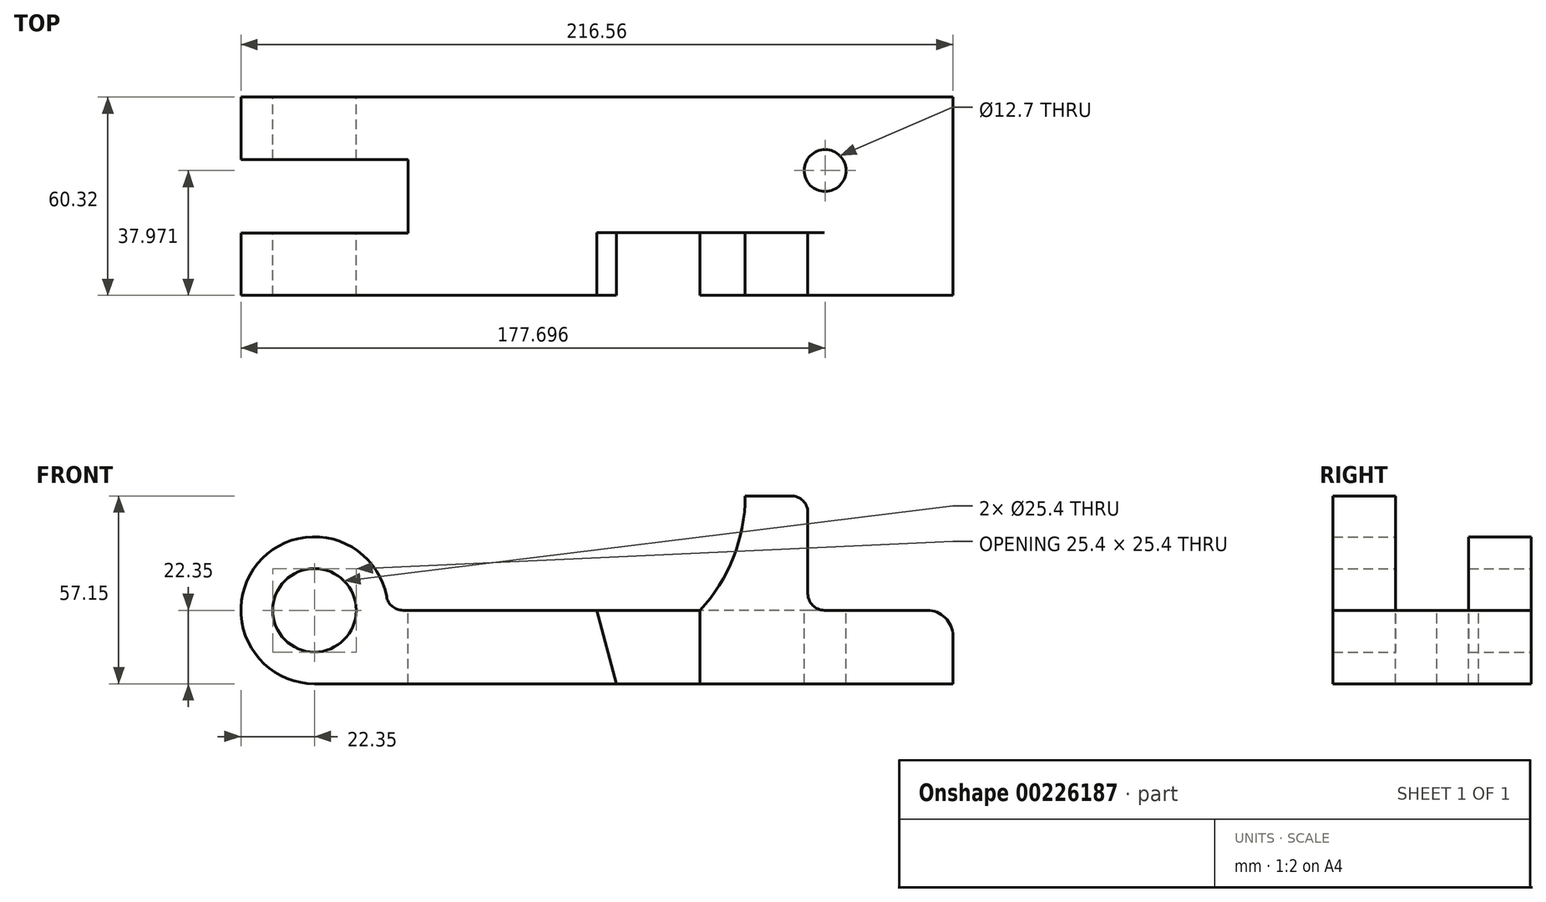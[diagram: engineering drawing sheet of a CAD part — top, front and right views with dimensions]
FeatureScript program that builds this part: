
annotation { "Feature Type Name" : "Feature", "Feature Type Description" : "" }
export const myFeature = defineFeature(function(context is Context, id is Id, definition is map)
    precondition{}
    {
        {
            var Q0;
            Q0=qCreatedBy(makeId("Front.planeOp"),FACE);
            var sketch = newSketch(context, id + "F0", { "sketchPlane" : qUnion([Q0])});
            skCircle(sketch, "E0", {"center": v(0, 0) * mm, "radius": 12.7 * mm});
            skArc(sketch, "E1", {"start": v(22.35, 0) * mm, "mid": v(-15.8, 15.8) * mm, "end": v(0, -22.35) * mm});
            skLineSegment(sketch, "E2", {"start": v(0, -22.35) * mm, "end": v(91.85, -22.35) * mm});
            skLineSegment(sketch, "E3", {"start": v(91.85, -22.35) * mm, "end": v(117.25, -22.35) * mm});
            skLineSegment(sketch, "E4", {"start": v(117.25, -22.35) * mm, "end": v(194.2, -22.35) * mm});
            skLineSegment(sketch, "E5", {"start": v(194.2, -22.35) * mm, "end": v(194.2, 0) * mm});
            skLineSegment(sketch, "E6", {"start": v(22.35, 0) * mm, "end": v(85.85, 0) * mm});
            skLineSegment(sketch, "E7", {"start": v(194.2, 0) * mm, "end": v(150.09, 0) * mm});
            skLineSegment(sketch, "E8", {"start": v(150.09, 0) * mm, "end": v(150.09, 34.8) * mm});
            skLineSegment(sketch, "E9", {"start": v(150.09, 34.8) * mm, "end": v(131.04, 34.8) * mm});
            skLineSegment(sketch, "E10", {"start": v(117.25, -22.35) * mm, "end": v(117.25, 0) * mm});
            skLineSegment(sketch, "E11", {"start": v(85.85, 0) * mm, "end": v(117.25, 0) * mm});
            skLineSegment(sketch, "E12", {"start": v(91.85, -22.35) * mm, "end": v(85.85, 0) * mm});
            skArc(sketch, "E13", {"start": v(117.25, 0) * mm, "mid": v(127.46, 16.08) * mm, "end": v(131.04, 34.8) * mm});
            skSolve(sketch);
        }
        {
            var Q0;
            Q0=makeQuery(id+"F0.imprint","IMPRINT",FACE,{"disambiguationData":[TD([[makeQuery(id+"F0.imprint","IMPRINT",EDGE,{"derivedFrom":sQuery(id+"F0.wireOp",EDGE,"E0")}),-1.0]])]});
            var Q1;
            Q1=makeQuery(id+"F0.imprint","IMPRINT",FACE,{"disambiguationData":[TD([[makeQuery(id+"F0.imprint","IMPRINT",EDGE,{"derivedFrom":sQuery(id+"F0.wireOp",EDGE,"E4")}),1.0]])]});
            var Q2;
            Q2=makeQuery(id+"F0.imprint","IMPRINT",FACE,{"disambiguationData":[TD([[makeQuery(id+"F0.imprint","IMPRINT",EDGE,{"derivedFrom":sQuery(id+"F0.wireOp",EDGE,"E3")}),1.0]])]});
            extrude(context, id + "F11", {"entities" : qUnion([Q0, Q1, Q2]), "endBound" : BoundingType.SYMMETRIC, "depth" : 60.32 * mm});
        }
        {
            var Q0;
            Q0=makeQuery(id+"F11.opExtrude","CAP_FACE",FACE,{"disambiguationData":[OSD([sQuery(id+"F0.wireOp",EDGE,"E0"),sQuery(id+"F0.wireOp",EDGE,"E1"),sQuery(id+"F0.wireOp",EDGE,"E2"),sQuery(id+"F0.wireOp",EDGE,"E3"),sQuery(id+"F0.wireOp",EDGE,"E4"),sQuery(id+"F0.wireOp",EDGE,"E5"),sQuery(id+"F0.wireOp",EDGE,"E6"),sQuery(id+"F0.wireOp",EDGE,"E7"),sQuery(id+"F0.wireOp",EDGE,"E8"),sQuery(id+"F0.wireOp",EDGE,"E9"),sQuery(id+"F0.wireOp",EDGE,"E11"),sQuery(id+"F0.wireOp",EDGE,"E13")])],"isStart":false});
            var sketch = newSketch(context, id + "F1", { "sketchPlane" : qUnion([Q0])});
            skPoint(sketch, "E14.0", {"position": v(91.85, -22.35) * mm});
            skPoint(sketch, "E15.0", {"position": v(85.85, 0) * mm});
            skPoint(sketch, "E16.0", {"position": v(117.25, -22.35) * mm});
            skPoint(sketch, "E17.0", {"position": v(117.25, 0) * mm});
            skLineSegment(sketch, "E18.0", {"start": v(85.85, 0) * mm, "end": v(117.25, 0) * mm});
            skLineSegment(sketch, "E19.0", {"start": v(91.85, -22.35) * mm, "end": v(117.25, -22.35) * mm});
            skLineSegment(sketch, "E20", {"start": v(91.85, -22.35) * mm, "end": v(85.85, 0) * mm});
            skLineSegment(sketch, "E21", {"start": v(117.25, -22.35) * mm, "end": v(117.25, 0) * mm});
            skSolve(sketch);
        }
        {
            var Q0;
            Q0 = qSketchRegion(id + "F1", true);
            extrude(context, id + "F2", {"entities" : qUnion([Q0]), "operationType" : NewBodyOperationType.REMOVE, "oppositeDirection" : true, "depth" : 19.05 * mm});
        }
        {
            var Q0;
            Q0=makeQuery(id+"F11.opExtrude","CAP_FACE",FACE,{"disambiguationData":[OSD([sQuery(id+"F0.wireOp",EDGE,"E0"),sQuery(id+"F0.wireOp",EDGE,"E1"),sQuery(id+"F0.wireOp",EDGE,"E2"),sQuery(id+"F0.wireOp",EDGE,"E3"),sQuery(id+"F0.wireOp",EDGE,"E4"),sQuery(id+"F0.wireOp",EDGE,"E5"),sQuery(id+"F0.wireOp",EDGE,"E6"),sQuery(id+"F0.wireOp",EDGE,"E7"),sQuery(id+"F0.wireOp",EDGE,"E8"),sQuery(id+"F0.wireOp",EDGE,"E9"),sQuery(id+"F0.wireOp",EDGE,"E11"),sQuery(id+"F0.wireOp",EDGE,"E13")])],"isStart":true});
            var sketch = newSketch(context, id + "F3", { "sketchPlane" : qUnion([Q0])});
            skPoint(sketch, "E22.0", {"position": v(-150.09, 0) * mm});
            skPoint(sketch, "E23.0", {"position": v(-117.25, 0) * mm});
            skLineSegment(sketch, "E24", {"start": v(-150.09, 0) * mm, "end": v(-117.25, 0) * mm});
            skSolve(sketch);
        }
        {
            var Q0;
            Q0 = qSketchRegion(id + "F3", true);
            var Q1;
            Q1=makeQuery(id+"F3.imprint","IMPRINT",FACE,{"disambiguationData":[TD([[makeQuery(id+"F3.imprint","IMPRINT",EDGE,{"derivedFrom":sQuery(id+"F3.wireOp",EDGE,"E24")}),1.0]])]});
            extrude(context, id + "F4", {"entities" : qUnion([Q0, Q1]), "operationType" : NewBodyOperationType.REMOVE, "oppositeDirection" : true, "depth" : 41.27 * mm});
        }
        {
            var Q0;
            Q0=makeQuery(id+"F11.opExtrude","SWEPT_EDGE",EDGE,{"disambiguationData":[OSD([sQuery(id+"F0.wireOp",EDGE,"E1"),sQuery(id+"F0.wireOp",EDGE,"E6")])]});
            var Q1;
            Q1=makeQuery(id+"F11.opExtrude","SWEPT_EDGE",EDGE,{"disambiguationData":[OSD([sQuery(id+"F0.wireOp",EDGE,"E8"),sQuery(id+"F0.wireOp",EDGE,"E9")])]});
            var Q2;
            Q2=makeQuery(id+"F11.opExtrude","SWEPT_EDGE",EDGE,{"disambiguationData":[OSD([sQuery(id+"F0.wireOp",EDGE,"E7"),sQuery(id+"F0.wireOp",EDGE,"E8")])]});
            fillet(context, id + "F5", {"entities" : qUnion([Q0, Q1, Q2]), "radius" : 5.08 * mm, "tangentPropagation" : true, "allowEdgeOverflow" : false});
        }
        {
            var Q0;
            Q0=makeQuery(id+"F11.opExtrude","SWEPT_EDGE",EDGE,{"disambiguationData":[OSD([sQuery(id+"F0.wireOp",EDGE,"E5"),sQuery(id+"F0.wireOp",EDGE,"E7")])]});
            fillet(context, id + "F6", {"entities" : qUnion([Q0]), "radius" : 7.87 * mm, "tangentPropagation" : true, "allowEdgeOverflow" : false});
        }
        {
            var Q0;
            Q0=qCreatedBy(makeId("Top.planeOp"),FACE);
            var sketch = newSketch(context, id + "F7", { "sketchPlane" : qUnion([Q0])});
            skLineSegment(sketch, "E25", {"start": v(-22.35, -30.16) * mm, "end": v(-22.35, 30.16) * mm});
            skLineSegment(sketch, "E26.0", {"start": v(186.33, 30.16) * mm, "end": v(26.96, 30.16) * mm});
            skLineSegment(sketch, "E27.0", {"start": v(26.96, -30.16) * mm, "end": v(85.85, -30.16) * mm});
            skLineSegment(sketch, "E28", {"start": v(28.45, 30.16) * mm, "end": v(28.45, -30.16) * mm});
            skLineSegment(sketch, "E29", {"start": v(28.45, 11.16) * mm, "end": v(-22.35, 11.16) * mm});
            skLineSegment(sketch, "E30", {"start": v(28.45, -11.16) * mm, "end": v(-22.35, -11.16) * mm});
            skSolve(sketch);
        }
        {
            var Q0;
            {var subQ0=sQuery(id+"F7.wireOp",EDGE,"E29");Q0=makeQuery(id+"F7.imprint","IMPRINT",FACE,{"disambiguationData":[TD([[makeQuery(id+"F7.imprint","IMPRINT",EDGE,{"derivedFrom":subQ0}),1.0]])]});}
            extrude(context, id + "F8", {"entities" : qUnion([Q0]), "operationType" : NewBodyOperationType.REMOVE, "endBound" : BoundingType.SYMMETRIC, "oppositeDirection" : true, "depth" : 76.2 * mm});
        }
        {
            var Q0;
            Q0=makeQuery(id+"F4.boolean.opBoolean","MERGE",FACE,{"derivedFrom":[makeQuery(id+"F11.opExtrude","SWEPT_FACE",FACE,{"disambiguationData":[OSD([sQuery(id+"F0.wireOp",EDGE,"E7")])]}),makeQuery(id+"F11.opExtrude","SWEPT_FACE",FACE,{"disambiguationData":[OSD([sQuery(id+"F0.wireOp",EDGE,"E6"),sQuery(id+"F0.wireOp",EDGE,"E11")])]}),makeQuery(id+"F4.opExtrude","SWEPT_FACE",FACE,{"disambiguationData":[OSD([sQuery(id+"F3.wireOp",EDGE,"E24")])]})]});
            var sketch = newSketch(context, id + "F9", { "sketchPlane" : qUnion([Q0])});
            skCircle(sketch, "E31", {"center": v(155.35, 7.81) * mm, "radius": 6.35 * mm});
            skSolve(sketch);
        }
        {
            var Q0;
            Q0 = qSketchRegion(id + "F9", true);
            extrude(context, id + "F10", {"entities" : qUnion([Q0]), "operationType" : NewBodyOperationType.REMOVE, "endBound" : BoundingType.THROUGH_ALL, "oppositeDirection" : true, "depth" : 25.4 * mm});
        }
    });
